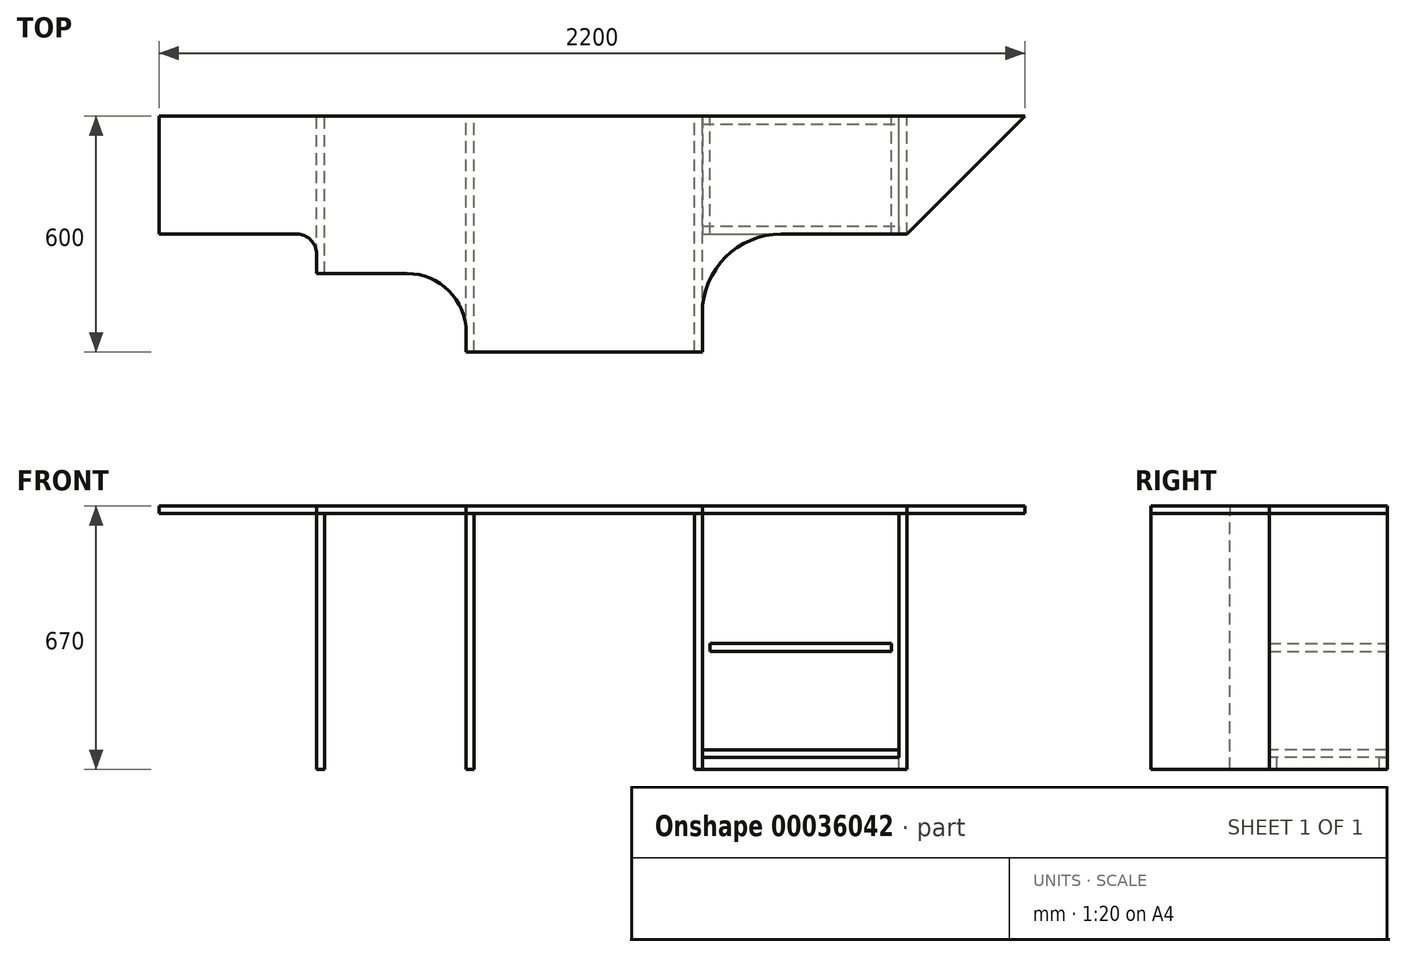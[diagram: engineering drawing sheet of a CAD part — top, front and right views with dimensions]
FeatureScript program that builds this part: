
annotation { "Feature Type Name" : "Feature", "Feature Type Description" : "" }
export const myFeature = defineFeature(function(context is Context, id is Id, definition is map)
    precondition{}
    {
        {
            var Q0;
            Q0=qCreatedBy(makeId("Front.planeOp"),FACE);
            var sketch = newSketch(context, id + "F0", { "sketchPlane" : qUnion([Q0])});
            skLineSegment(sketch, "E0.bottom", {"start": v(-1100, 0) * mm, "end": v(1100, 0) * mm});
            skLineSegment(sketch, "E0.top", {"start": v(-1100, 2200) * mm, "end": v(1100, 2200) * mm});
            skLineSegment(sketch, "E0.left", {"start": v(-1100, 0) * mm, "end": v(-1100, 2200) * mm});
            skLineSegment(sketch, "E0.right", {"start": v(1100, 0) * mm, "end": v(1100, 2200) * mm});
            skSolve(sketch);
        }
        {
            var Q0;
            Q0=qCreatedBy(makeId("Front.planeOp"),FACE);
            var sketch = newSketch(context, id + "F1", { "sketchPlane" : qUnion([Q0])});
            skLineSegment(sketch, "E1", {"start": v(-320, 0) * mm, "end": v(-320, 650) * mm});
            skLineSegment(sketch, "E2", {"start": v(-320, 650) * mm, "end": v(-300, 650) * mm});
            skLineSegment(sketch, "E3", {"start": v(-300, 650) * mm, "end": v(-300, 0) * mm});
            skLineSegment(sketch, "E4", {"start": v(-300, 0) * mm, "end": v(-320, 0) * mm});
            skLineSegment(sketch, "E5", {"start": v(260, 0) * mm, "end": v(260, 650) * mm});
            skLineSegment(sketch, "E6", {"start": v(260, 650) * mm, "end": v(280, 650) * mm});
            skLineSegment(sketch, "E7", {"start": v(280, 650) * mm, "end": v(280, 0) * mm});
            skLineSegment(sketch, "E8", {"start": v(280, 0) * mm, "end": v(260, 0) * mm});
            skSolve(sketch);
        }
        {
            var Q0;
            Q0 = qSketchRegion(id + "F1", true);
            extrude(context, id + "F2", {"entities" : qUnion([Q0]), "depth" : 600 * mm});
        }
        {
            var Q0;
            Q0=makeQuery(id+"F0.imprint","IMPRINT",FACE,{"disambiguationData":[TD([[makeQuery(id+"F0.imprint","IMPRINT",EDGE,{"derivedFrom":sQuery(id+"F0.wireOp",EDGE,"E0.bottom")}),1.0]])]});
            var sketch = newSketch(context, id + "F3", { "sketchPlane" : qUnion([Q0])});
            skLineSegment(sketch, "E9.bottom", {"start": v(-680, 0) * mm, "end": v(-700, 0) * mm});
            skLineSegment(sketch, "E9.top", {"start": v(-680, 650) * mm, "end": v(-700, 650) * mm});
            skLineSegment(sketch, "E9.left", {"start": v(-680, 0) * mm, "end": v(-680, 650) * mm});
            skLineSegment(sketch, "E9.right", {"start": v(-700, 0) * mm, "end": v(-700, 650) * mm});
            skSolve(sketch);
        }
        {
            var Q0;
            Q0 = qSketchRegion(id + "F3", true);
            extrude(context, id + "F4", {"entities" : qUnion([Q0]), "depth" : 400 * mm});
        }
        {
            var Q0;
            Q0=makeQuery(id+"F0.imprint","IMPRINT",FACE,{"disambiguationData":[TD([[makeQuery(id+"F0.imprint","IMPRINT",EDGE,{"derivedFrom":sQuery(id+"F0.wireOp",EDGE,"E0.bottom")}),1.0]])]});
            var sketch = newSketch(context, id + "F5", { "sketchPlane" : qUnion([Q0])});
            skLineSegment(sketch, "E10.bottom", {"start": v(780, 0) * mm, "end": v(800, 0) * mm});
            skLineSegment(sketch, "E10.top", {"start": v(780, 650) * mm, "end": v(800, 650) * mm});
            skLineSegment(sketch, "E10.left", {"start": v(780, 0) * mm, "end": v(780, 650) * mm});
            skLineSegment(sketch, "E10.right", {"start": v(800, 0) * mm, "end": v(800, 650) * mm});
            skSolve(sketch);
        }
        {
            var Q0;
            Q0 = qSketchRegion(id + "F5", true);
            extrude(context, id + "F6", {"entities" : qUnion([Q0]), "depth" : 300 * mm});
        }
        {
            var Q0;
            Q0=makeQuery(id+"F2.opExtrude","SWEPT_FACE",FACE,{"disambiguationData":[OSD([sQuery(id+"F1.wireOp",EDGE,"E2")])]});
            var sketch = newSketch(context, id + "F7", { "sketchPlane" : qUnion([Q0])});
            skPoint(sketch, "E11.0", {"position": v(800, -300) * mm});
            skPoint(sketch, "E12.0", {"position": v(280, -600) * mm});
            skPoint(sketch, "E13.0", {"position": v(-320, -600) * mm});
            skPoint(sketch, "E14.0", {"position": v(-700, -400) * mm});
            skPoint(sketch, "E15.0", {"position": v(-1100, 0) * mm});
            skPoint(sketch, "E16.0", {"position": v(1100, 0) * mm});
            skLineSegment(sketch, "E17", {"start": v(1100, 0) * mm, "end": v(-1100, 0) * mm});
            skLineSegment(sketch, "E18", {"start": v(1100, 0) * mm, "end": v(800, -300) * mm});
            skLineSegment(sketch, "E19", {"start": v(-1100, 0) * mm, "end": v(-1100, -300) * mm});
            skLineSegment(sketch, "E20", {"start": v(-1100, -300) * mm, "end": v(-750, -300) * mm});
            skLineSegment(sketch, "E21", {"start": v(-700, -350) * mm, "end": v(-700, -400) * mm});
            skLineSegment(sketch, "E22", {"start": v(-700, -400) * mm, "end": v(-470, -400) * mm});
            skLineSegment(sketch, "E23", {"start": v(-320, -550) * mm, "end": v(-320, -600) * mm});
            skLineSegment(sketch, "E24", {"start": v(-320, -600) * mm, "end": v(280, -600) * mm});
            skLineSegment(sketch, "E25", {"start": v(800, -300) * mm, "end": v(480, -300) * mm});
            skLineSegment(sketch, "E26", {"start": v(280, -500) * mm, "end": v(280, -600) * mm});
            skPoint(sketch, "E27.visualSharp", {"position": v(280, -300) * mm});
            skArc(sketch, "E27.filletArc", {"start": v(480, -300) * mm, "mid": v(338.58, -358.58) * mm, "end": v(280, -500) * mm});
            skPoint(sketch, "E28.visualSharp", {"position": v(-320, -400) * mm});
            skArc(sketch, "E28.filletArc", {"start": v(-320, -550) * mm, "mid": v(-363.93, -443.93) * mm, "end": v(-470, -400) * mm});
            skPoint(sketch, "E29.visualSharp", {"position": v(-700, -300) * mm});
            skArc(sketch, "E29.filletArc", {"start": v(-700, -350) * mm, "mid": v(-714.64, -314.64) * mm, "end": v(-750, -300) * mm});
            skSolve(sketch);
        }
        {
            var Q0;
            Q0 = qSketchRegion(id + "F7", true);
            extrude(context, id + "F8", {"entities" : qUnion([Q0]), "depth" : 20 * mm});
        }
        {
            var Q0;
            Q0=qCreatedBy(makeId("Front.planeOp"),FACE);
            var sketch = newSketch(context, id + "F9", { "sketchPlane" : qUnion([Q0])});
            skPoint(sketch, "E30.0", {"position": v(780, 0) * mm});
            skPoint(sketch, "E31.0", {"position": v(280, 0) * mm});
            skLineSegment(sketch, "E32.bottom", {"start": v(280, 0) * mm, "end": v(780, 0) * mm});
            skLineSegment(sketch, "E32.top", {"start": v(280, 30) * mm, "end": v(780, 30) * mm});
            skLineSegment(sketch, "E32.left", {"start": v(280, 0) * mm, "end": v(280, 30) * mm});
            skLineSegment(sketch, "E32.right", {"start": v(780, 0) * mm, "end": v(780, 30) * mm});
            skSolve(sketch);
        }
        {
            var Q0;
            Q0 = qSketchRegion(id + "F9", true);
            extrude(context, id + "F10", {"entities" : qUnion([Q0]), "depth" : 20 * mm});
        }
        {
            var Q0;
            Q0=makeQuery(id+"F6.opExtrude","CAP_FACE",FACE,{"disambiguationData":[OSD([sQuery(id+"F5.wireOp",EDGE,"E10.bottom"),sQuery(id+"F5.wireOp",EDGE,"E10.top"),sQuery(id+"F5.wireOp",EDGE,"E10.left"),sQuery(id+"F5.wireOp",EDGE,"E10.right")])],"isStart":false});
            var sketch = newSketch(context, id + "F11", { "sketchPlane" : qUnion([Q0])});
            skPoint(sketch, "E33.0", {"position": v(280, 0) * mm});
            skPoint(sketch, "E34.0", {"position": v(780, 0) * mm});
            skLineSegment(sketch, "E35.bottom", {"start": v(280, 0) * mm, "end": v(780, 0) * mm});
            skLineSegment(sketch, "E35.top", {"start": v(280, 30) * mm, "end": v(780, 30) * mm});
            skLineSegment(sketch, "E35.left", {"start": v(280, 0) * mm, "end": v(280, 30) * mm});
            skLineSegment(sketch, "E35.right", {"start": v(780, 0) * mm, "end": v(780, 30) * mm});
            skSolve(sketch);
        }
        {
            var Q0;
            Q0 = qSketchRegion(id + "F11", true);
            extrude(context, id + "F12", {"entities" : qUnion([Q0]), "operationType" : NewBodyOperationType.ADD, "oppositeDirection" : true, "depth" : 20 * mm});
        }
        {
            var Q0;
            Q0=makeQuery(id+"F12.opExtrude","SWEPT_FACE",FACE,{"disambiguationData":[OSD([sQuery(id+"F11.wireOp",EDGE,"E35.top")])]});
            var sketch = newSketch(context, id + "F13", { "sketchPlane" : qUnion([Q0])});
            skPoint(sketch, "E36.0", {"position": v(280, -300) * mm});
            skPoint(sketch, "E37.0", {"position": v(280, 0) * mm});
            skPoint(sketch, "E38.0", {"position": v(780, -300) * mm});
            skLineSegment(sketch, "E39.bottom", {"start": v(280, 0) * mm, "end": v(780, 0) * mm});
            skLineSegment(sketch, "E39.top", {"start": v(280, -300) * mm, "end": v(780, -300) * mm});
            skLineSegment(sketch, "E39.left", {"start": v(280, 0) * mm, "end": v(280, -300) * mm});
            skLineSegment(sketch, "E39.right", {"start": v(780, 0) * mm, "end": v(780, -300) * mm});
            skSolve(sketch);
        }
        {
            var Q0;
            Q0 = qSketchRegion(id + "F13", true);
            extrude(context, id + "F14", {"entities" : qUnion([Q0]), "depth" : 20 * mm});
        }
        {
            var Q0;
            Q0=qCreatedBy(makeId("Front.planeOp"),FACE);
            var sketch = newSketch(context, id + "F15", { "sketchPlane" : qUnion([Q0])});
            skLineSegment(sketch, "E40.bottom", {"start": v(300, 320) * mm, "end": v(760, 320) * mm});
            skLineSegment(sketch, "E40.top", {"start": v(300, 300) * mm, "end": v(760, 300) * mm});
            skLineSegment(sketch, "E40.left", {"start": v(300, 320) * mm, "end": v(300, 300) * mm});
            skLineSegment(sketch, "E40.right", {"start": v(760, 320) * mm, "end": v(760, 300) * mm});
            skSolve(sketch);
        }
        {
            var Q0;
            Q0 = qSketchRegion(id + "F15", true);
            extrude(context, id + "F16", {"entities" : qUnion([Q0]), "depth" : 300 * mm});
        }
    });
